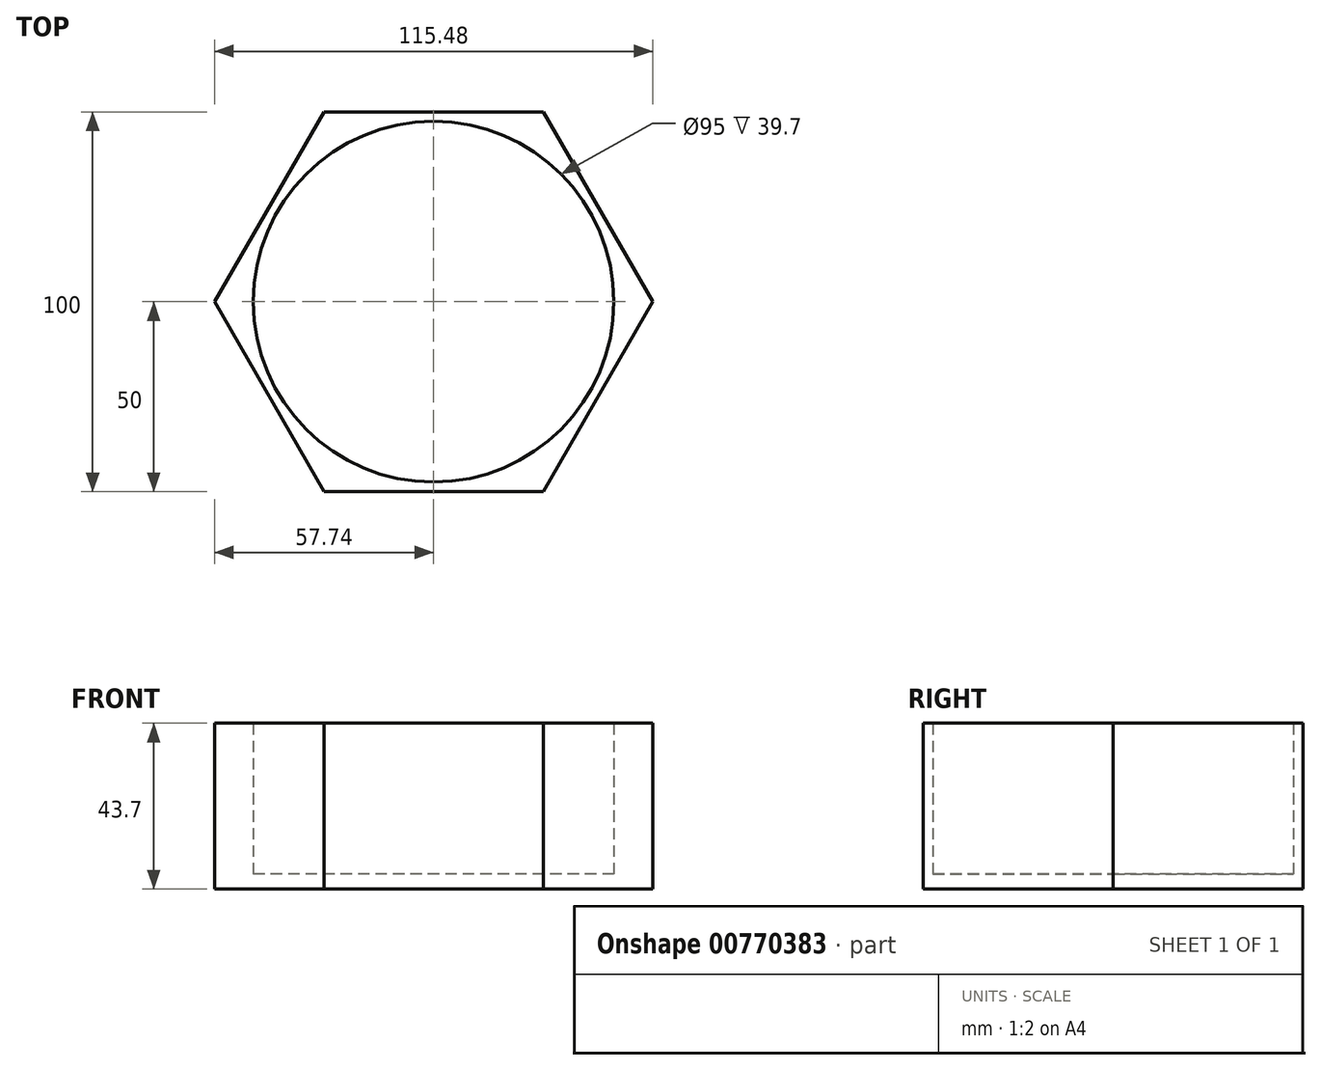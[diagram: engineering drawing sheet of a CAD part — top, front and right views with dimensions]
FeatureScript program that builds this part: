
annotation { "Feature Type Name" : "Feature", "Feature Type Description" : "" }
export const myFeature = defineFeature(function(context is Context, id is Id, definition is map)
    precondition{}
    {
        {
            var Q0;
            Q0=qCreatedBy(makeId("Top.planeOp"),FACE);
            var sketch = newSketch(context, id + "F0", { "sketchPlane" : qUnion([Q0])});
            skCircle(sketch, "E0.cCircle", {"center": v(0, 0) * mm, "radius": 50 * mm, "construction": true});
            skLineSegment(sketch, "E0.0", {"start": v(-28.87, 50) * mm, "end": v(28.87, 50) * mm});
            skLineSegment(sketch, "E0.1", {"start": v(28.87, 50) * mm, "end": v(57.74, 0) * mm});
            skLineSegment(sketch, "E0.2", {"start": v(57.74, 0) * mm, "end": v(28.87, -50) * mm});
            skLineSegment(sketch, "E0.3", {"start": v(28.87, -50) * mm, "end": v(-28.87, -50) * mm});
            skLineSegment(sketch, "E0.4", {"start": v(-28.87, -50) * mm, "end": v(-57.74, 0) * mm});
            skLineSegment(sketch, "E0.5", {"start": v(-57.74, 0) * mm, "end": v(-28.87, 50) * mm});
            skPoint(sketch, "E0.0.midPoint", {"position": v(0, 50) * mm});
            skSolve(sketch);
        }
        {
            var Q0;
            Q0=makeQuery(id+"F0.imprint","IMPRINT",FACE,{"disambiguationData":[TD([[makeQuery(id+"F0.imprint","IMPRINT",EDGE,{"derivedFrom":sQuery(id+"F0.wireOp",EDGE,"E0.0")}),-1.0]])]});
            extrude(context, id + "F1", {"entities" : qUnion([Q0]), "depth" : 4 * mm, "offsetDistance" : 25 * mm});
        }
        {
            var Q0;
            Q0=makeQuery(id+"F1.opExtrude","CAP_FACE",FACE,{"disambiguationData":[OSD([sQuery(id+"F0.wireOp",EDGE,"E0.0"),sQuery(id+"F0.wireOp",EDGE,"E0.1"),sQuery(id+"F0.wireOp",EDGE,"E0.2"),sQuery(id+"F0.wireOp",EDGE,"E0.3"),sQuery(id+"F0.wireOp",EDGE,"E0.4"),sQuery(id+"F0.wireOp",EDGE,"E0.5")])],"isStart":false});
            var sketch = newSketch(context, id + "F2", { "sketchPlane" : qUnion([Q0])});
            skCircle(sketch, "E1.cCircle", {"center": v(0, 0) * mm, "radius": 50 * mm, "construction": true});
            skPoint(sketch, "E1.cCircle.perimeterSnap0", {"position": v(0, 50) * mm});
            skLineSegment(sketch, "E1.0", {"start": v(-28.87, 50) * mm, "end": v(28.87, 50) * mm});
            skLineSegment(sketch, "E1.1", {"start": v(28.87, 50) * mm, "end": v(57.74, 0) * mm});
            skLineSegment(sketch, "E1.2", {"start": v(57.74, 0) * mm, "end": v(28.87, -50) * mm});
            skLineSegment(sketch, "E1.3", {"start": v(28.87, -50) * mm, "end": v(-28.87, -50) * mm});
            skLineSegment(sketch, "E1.4", {"start": v(-28.87, -50) * mm, "end": v(-57.74, 0) * mm});
            skLineSegment(sketch, "E1.5", {"start": v(-57.74, 0) * mm, "end": v(-28.87, 50) * mm});
            skPoint(sketch, "E1.0.midPoint", {"position": v(0, 50) * mm});
            skPoint(sketch, "E1.0.midPoint.positionSnap0", {"position": v(0, 50) * mm});
            skSolve(sketch);
        }
        {
            var Q0;
            Q0=makeQuery(id+"F2.imprint","IMPRINT",FACE,{"disambiguationData":[TD([[makeQuery(id+"F2.imprint","IMPRINT",EDGE,{"derivedFrom":sQuery(id+"F2.wireOp",EDGE,"E1.0")}),-1.0]])]});
            var sketch = newSketch(context, id + "F3", { "sketchPlane" : qUnion([Q0])});
            skCircle(sketch, "E2", {"center": v(0, 0) * mm, "radius": 47.5 * mm});
            skSolve(sketch);
        }
        {
            var Q0;
            Q0=makeQuery(id+"F3.imprint","IMPRINT",FACE,{"disambiguationData":[TD([[makeQuery(id+"F3.imprint","IMPRINT",EDGE,{"derivedFrom":sQuery(id+"F3.wireOp",EDGE,"E2")}),-1.0]])]});
            extrude(context, id + "F4", {"entities" : qUnion([Q0]), "operationType" : NewBodyOperationType.ADD, "depth" : 39.7 * mm, "offsetDistance" : 25 * mm});
        }
    });
